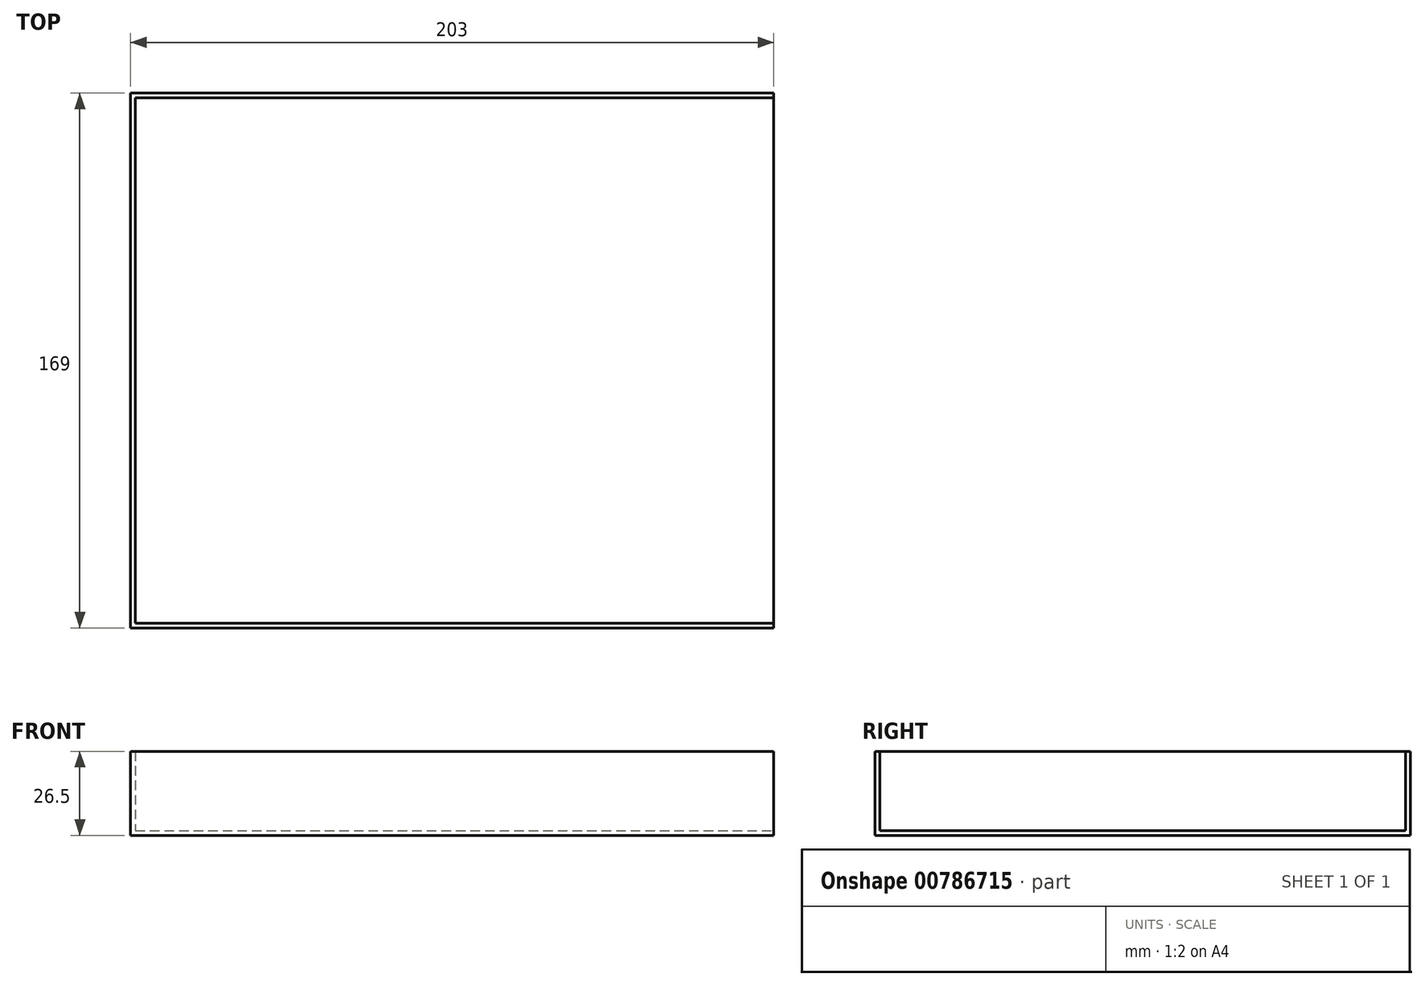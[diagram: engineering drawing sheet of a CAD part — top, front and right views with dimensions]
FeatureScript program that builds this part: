
annotation { "Feature Type Name" : "Feature", "Feature Type Description" : "" }
export const myFeature = defineFeature(function(context is Context, id is Id, definition is map)
    precondition{}
    {
        {
            var Q0;
            Q0=qCreatedBy(makeId("Top.planeOp"),FACE);
            var sketch = newSketch(context, id + "F0", { "sketchPlane" : qUnion([Q0])});
            skLineSegment(sketch, "E0.bottom", {"start": v(0, 0) * mm, "end": v(203, 0) * mm});
            skLineSegment(sketch, "E0.top", {"start": v(0, 169) * mm, "end": v(203, 169) * mm});
            skLineSegment(sketch, "E0.left", {"start": v(0, 0) * mm, "end": v(0, 169) * mm});
            skLineSegment(sketch, "E0.right", {"start": v(203, 0) * mm, "end": v(203, 169) * mm});
            skSolve(sketch);
        }
        {
            var Q0;
            Q0=makeQuery(id+"F0.imprint","IMPRINT",FACE,{"disambiguationData":[TD([[makeQuery(id+"F0.imprint","IMPRINT",EDGE,{"derivedFrom":sQuery(id+"F0.wireOp",EDGE,"E0.bottom")}),1.0]])]});
            extrude(context, id + "F1", {"entities" : qUnion([Q0]), "depth" : 1.5 * mm, "offsetDistance" : 25 * mm});
        }
        {
            var Q0;
            Q0=makeQuery(id+"F1.opExtrude","CAP_FACE",FACE,{"disambiguationData":[OSD([sQuery(id+"F0.wireOp",EDGE,"E0.bottom"),sQuery(id+"F0.wireOp",EDGE,"E0.top"),sQuery(id+"F0.wireOp",EDGE,"E0.left"),sQuery(id+"F0.wireOp",EDGE,"E0.right")])],"isStart":false});
            var sketch = newSketch(context, id + "F2", { "sketchPlane" : qUnion([Q0])});
            skLineSegment(sketch, "E1.bottom", {"start": v(0, 169) * mm, "end": v(1.5, 169) * mm});
            skLineSegment(sketch, "E1.top", {"start": v(0, 0) * mm, "end": v(1.5, 0) * mm});
            skLineSegment(sketch, "E1.left", {"start": v(0, 169) * mm, "end": v(0, 0) * mm});
            skLineSegment(sketch, "E1.right", {"start": v(1.5, 169) * mm, "end": v(1.5, 0) * mm});
            skLineSegment(sketch, "E2.bottom", {"start": v(1.5, 0) * mm, "end": v(203, 0) * mm});
            skLineSegment(sketch, "E2.top", {"start": v(1.5, 1.5) * mm, "end": v(203, 1.5) * mm});
            skLineSegment(sketch, "E2.left", {"start": v(1.5, 0) * mm, "end": v(1.5, 1.5) * mm});
            skLineSegment(sketch, "E2.right", {"start": v(203, 0) * mm, "end": v(203, 1.5) * mm});
            skLineSegment(sketch, "E3.bottom", {"start": v(1.5, 169) * mm, "end": v(203, 169) * mm});
            skLineSegment(sketch, "E3.top", {"start": v(1.5, 167.5) * mm, "end": v(203, 167.5) * mm});
            skLineSegment(sketch, "E3.left", {"start": v(1.5, 169) * mm, "end": v(1.5, 167.5) * mm});
            skLineSegment(sketch, "E3.right", {"start": v(203, 169) * mm, "end": v(203, 167.5) * mm});
            skSolve(sketch);
        }
        {
            var Q0;
            Q0=makeQuery(id+"F2.imprint","IMPRINT",FACE,{"disambiguationData":[TD([[makeQuery(id+"F2.imprint","IMPRINT",EDGE,{"derivedFrom":sQuery(id+"F2.wireOp",EDGE,"E1.bottom")}),-1.0]])]});
            var Q1;
            Q1=makeQuery(id+"F2.imprint","IMPRINT",FACE,{"disambiguationData":[TD([[makeQuery(id+"F2.imprint","IMPRINT",EDGE,{"derivedFrom":sQuery(id+"F2.wireOp",EDGE,"E2.bottom")}),1.0]])]});
            var Q2;
            Q2=makeQuery(id+"F2.imprint","IMPRINT",FACE,{"disambiguationData":[TD([[makeQuery(id+"F2.imprint","IMPRINT",EDGE,{"derivedFrom":sQuery(id+"F2.wireOp",EDGE,"E3.bottom")}),-1.0]])]});
            extrude(context, id + "F3", {"entities" : qUnion([Q0, Q1, Q2]), "operationType" : NewBodyOperationType.ADD, "depth" : 25 * mm, "offsetDistance" : 25 * mm});
        }
    });
